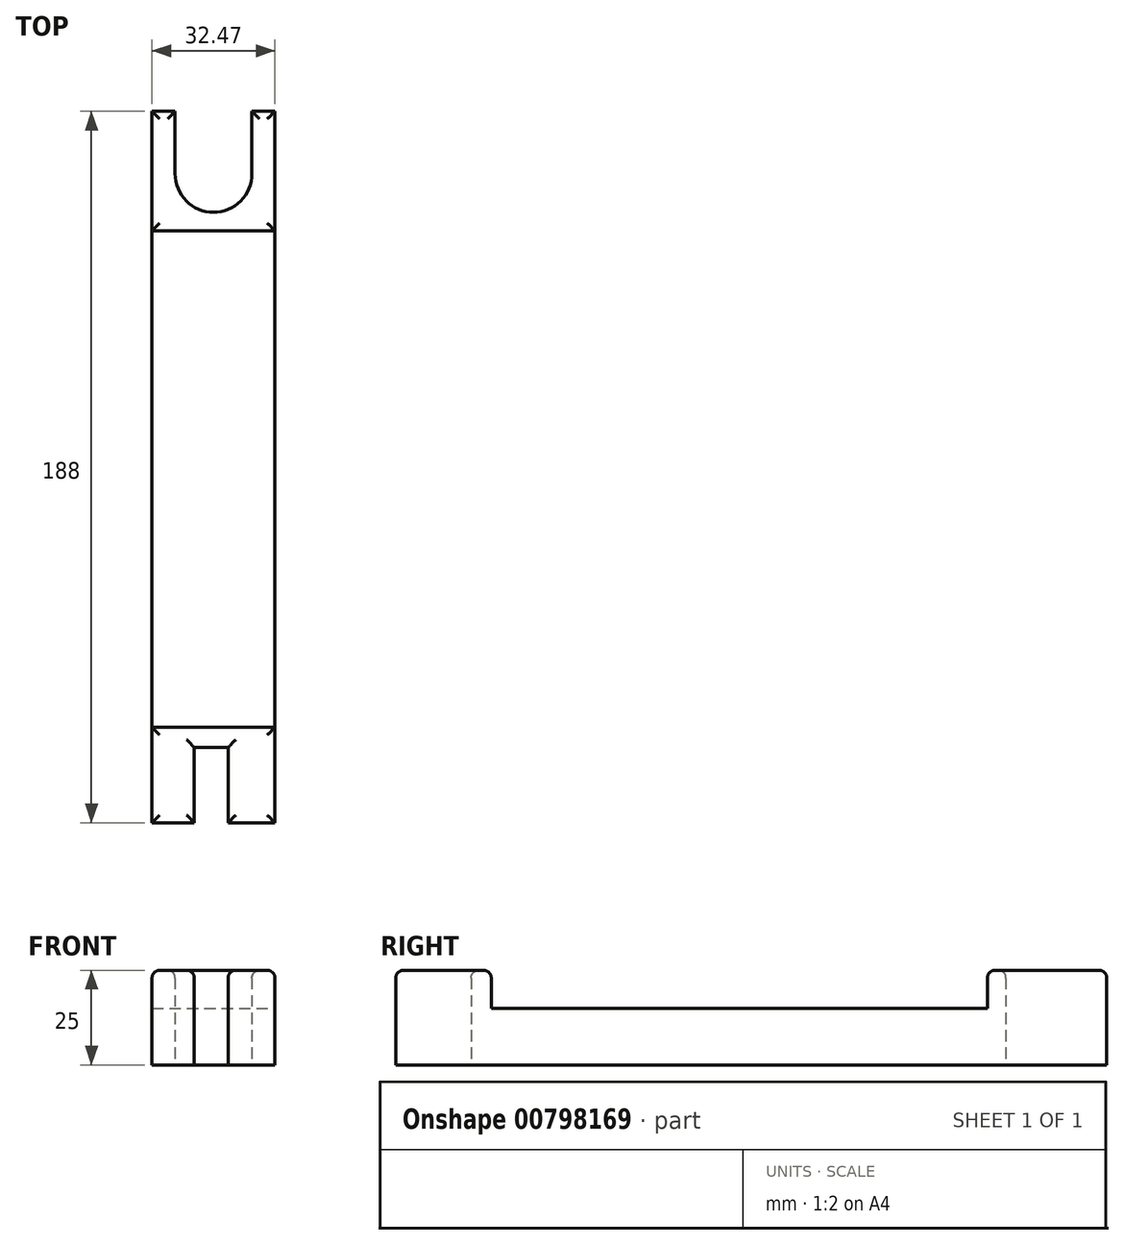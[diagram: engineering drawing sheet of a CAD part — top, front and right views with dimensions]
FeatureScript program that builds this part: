
annotation { "Feature Type Name" : "Feature", "Feature Type Description" : "" }
export const myFeature = defineFeature(function(context is Context, id is Id, definition is map)
    precondition{}
    {
        {
            var Q0;
            Q0=qCreatedBy(makeId("Top.planeOp"),FACE);
            var sketch = newSketch(context, id + "F0", { "sketchPlane" : qUnion([Q0])});
            skLineSegment(sketch, "E0.bottom", {"start": v(-15.1, 76.43) * mm, "end": v(17.37, 76.43) * mm});
            skLineSegment(sketch, "E0.top", {"start": v(-15.1, -69.85) * mm, "end": v(17.37, -69.85) * mm});
            skLineSegment(sketch, "E0.left", {"start": v(-15.1, 76.43) * mm, "end": v(-15.1, -69.85) * mm});
            skLineSegment(sketch, "E0.right", {"start": v(17.37, 76.43) * mm, "end": v(17.37, -69.85) * mm});
            skLineSegment(sketch, "E1.top", {"start": v(-15.1, -95.07) * mm, "end": v(17.37, -95.07) * mm});
            skLineSegment(sketch, "E1.left", {"start": v(-15.1, -69.85) * mm, "end": v(-15.1, -95.07) * mm});
            skLineSegment(sketch, "E1.right", {"start": v(17.37, -69.85) * mm, "end": v(17.37, -95.07) * mm});
            skLineSegment(sketch, "E2.bottom", {"start": v(-3.95, -95.07) * mm, "end": v(5.02, -95.07) * mm});
            skLineSegment(sketch, "E2.top", {"start": v(-3.95, -75.16) * mm, "end": v(5.02, -75.16) * mm});
            skLineSegment(sketch, "E2.left", {"start": v(-3.95, -95.07) * mm, "end": v(-3.95, -75.16) * mm});
            skLineSegment(sketch, "E2.right", {"start": v(5.02, -95.07) * mm, "end": v(5.02, -75.16) * mm});
            skCircle(sketch, "E3", {"center": v(1.14, 76.43) * mm, "radius": 10.16 * mm});
            skLineSegment(sketch, "E4.top", {"start": v(-15.1, 92.93) * mm, "end": v(17.37, 92.93) * mm});
            skLineSegment(sketch, "E4.left", {"start": v(-15.1, 76.43) * mm, "end": v(-15.1, 92.93) * mm});
            skLineSegment(sketch, "E4.right", {"start": v(17.37, 76.43) * mm, "end": v(17.37, 92.93) * mm});
            skPoint(sketch, "E5", {"position": v(-9.02, 76.43) * mm});
            skPoint(sketch, "E6", {"position": v(11.3, 76.43) * mm});
            skLineSegment(sketch, "E7", {"start": v(-9.02, 76.43) * mm, "end": v(-9.02, 92.93) * mm});
            skLineSegment(sketch, "E8", {"start": v(-9.02, 92.93) * mm, "end": v(11.3, 92.93) * mm});
            skLineSegment(sketch, "E9", {"start": v(11.3, 92.93) * mm, "end": v(11.3, 76.43) * mm});
            skLineSegment(sketch, "E10", {"start": v(-15.1, 61.37) * mm, "end": v(17.37, 61.37) * mm});
            skSolve(sketch);
        }
        {
            var Q0;
            Q0=makeQuery(id+"F0.imprint","IMPRINT",FACE,{"disambiguationData":[TD([[makeQuery(id+"F0.imprint","IMPRINT",EDGE,{"derivedFrom":sQuery(id+"F0.wireOp",EDGE,"E0.top")}),-1.0]])]});
            var Q1;
            {var subQ0=sQuery(id+"F0.wireOp",EDGE,"E10");Q1=makeQuery(id+"F0.imprint","IMPRINT",FACE,{"disambiguationData":[TD([[makeQuery(id+"F0.imprint","IMPRINT",EDGE,{"derivedFrom":subQ0}),1.0]])]});}
            var Q2;
            {var subQ0=sQuery(id+"F0.wireOp",EDGE,"E4.right");Q2=makeQuery(id+"F0.imprint","IMPRINT",FACE,{"disambiguationData":[TD([[makeQuery(id+"F0.imprint","IMPRINT",EDGE,{"derivedFrom":subQ0}),1.0]])]});}
            var Q3;
            {var subQ2=sQuery(id+"F0.wireOp",EDGE,"E4.left");Q3=makeQuery(id+"F0.imprint","IMPRINT",FACE,{"disambiguationData":[TD([[makeQuery(id+"F0.imprint","IMPRINT",EDGE,{"derivedFrom":subQ2}),-1.0]])]});}
            extrude(context, id + "F1", {"entities" : qUnion([Q0, Q1, Q2, Q3]), "depth" : 25 * mm, "offsetDistance" : 25 * mm});
        }
        {
            var Q0;
            {var subQ0=sQuery(id+"F0.wireOp",EDGE,"E0.top");Q0=makeQuery(id+"F0.imprint","IMPRINT",FACE,{"disambiguationData":[TD([[makeQuery(id+"F0.imprint","IMPRINT",EDGE,{"derivedFrom":subQ0}),1.0]])]});}
            extrude(context, id + "F2", {"entities" : qUnion([Q0]), "operationType" : NewBodyOperationType.ADD, "depth" : 15 * mm, "offsetDistance" : 25 * mm});
        }
        {
            var Q0;
            Q0=makeQuery(id+"F1.opExtrude","CAP_FACE",FACE,{"disambiguationData":[OSD([sQuery(id+"F0.wireOp",EDGE,"E0.left"),sQuery(id+"F0.wireOp",EDGE,"E0.right"),sQuery(id+"F0.wireOp",EDGE,"E3"),sQuery(id+"F0.wireOp",EDGE,"E4.top"),sQuery(id+"F0.wireOp",EDGE,"E4.left"),sQuery(id+"F0.wireOp",EDGE,"E4.right"),sQuery(id+"F0.wireOp",EDGE,"E7"),sQuery(id+"F0.wireOp",EDGE,"E9"),sQuery(id+"F0.wireOp",EDGE,"E10")])],"isStart":false});
            var Q1;
            Q1=makeQuery(id+"F1.opExtrude","CAP_FACE",FACE,{"disambiguationData":[OSD([sQuery(id+"F0.wireOp",EDGE,"E0.top"),sQuery(id+"F0.wireOp",EDGE,"E1.top"),sQuery(id+"F0.wireOp",EDGE,"E1.left"),sQuery(id+"F0.wireOp",EDGE,"E1.right"),sQuery(id+"F0.wireOp",EDGE,"E2.top"),sQuery(id+"F0.wireOp",EDGE,"E2.left"),sQuery(id+"F0.wireOp",EDGE,"E2.right")])],"isStart":false});
            fillet(context, id + "F3", {"entities" : qUnion([Q0, Q1]), "radius" : 2 * mm, "tangentPropagation" : true, "allowEdgeOverflow" : false});
        }
    });
